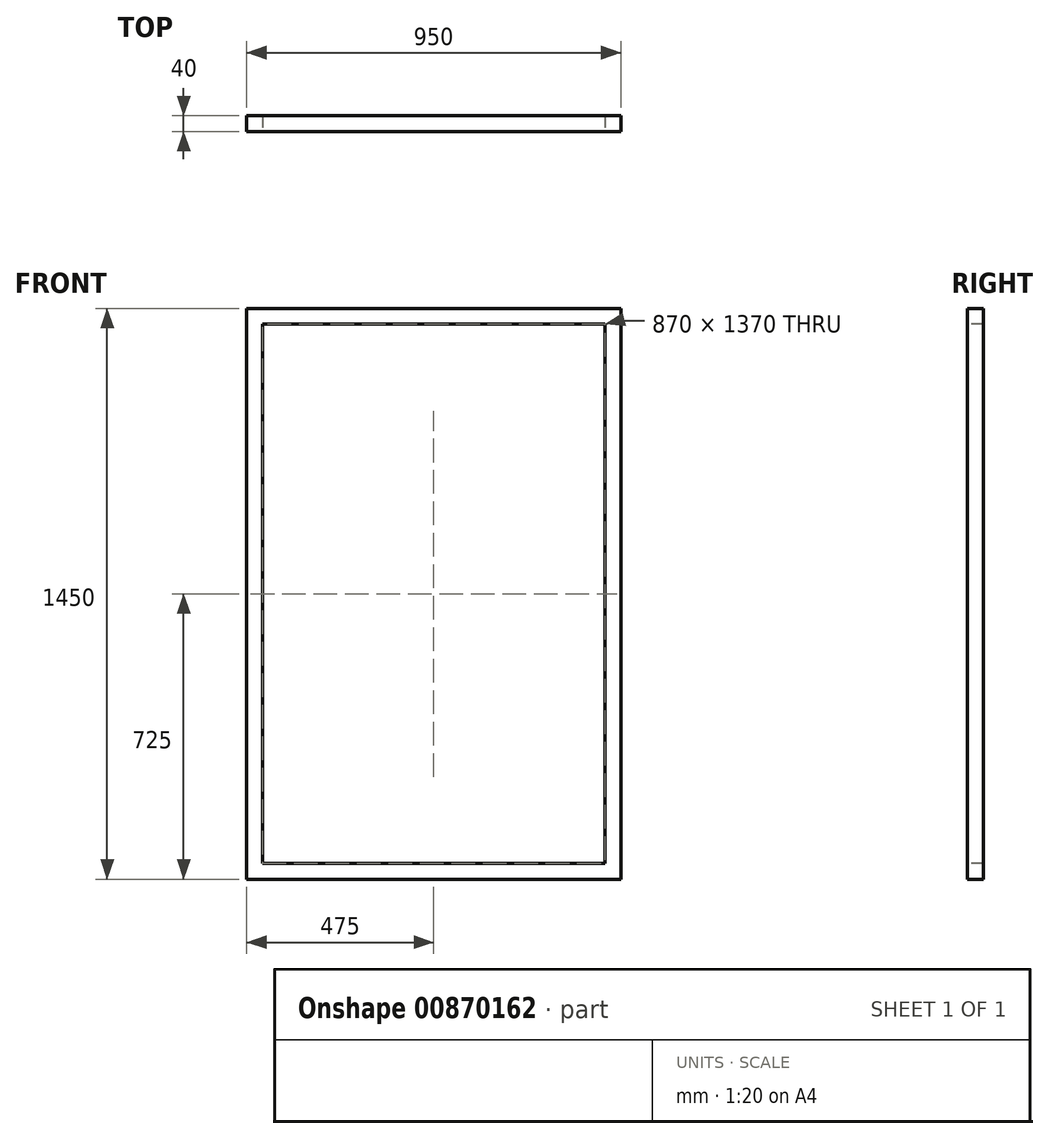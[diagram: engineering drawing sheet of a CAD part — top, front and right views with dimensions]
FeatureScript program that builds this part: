
annotation { "Feature Type Name" : "Feature", "Feature Type Description" : "" }
export const myFeature = defineFeature(function(context is Context, id is Id, definition is map)
    precondition{}
    {
        {
            var Q0;
            Q0=qCreatedBy(makeId("Front.planeOp"),FACE);
            var sketch = newSketch(context, id + "F0", { "sketchPlane" : qUnion([Q0])});
            skLineSegment(sketch, "E0.bottom", {"start": v(0, 0) * mm, "end": v(950, 0) * mm});
            skLineSegment(sketch, "E0.top", {"start": v(0, 1450) * mm, "end": v(950, 1450) * mm});
            skLineSegment(sketch, "E0.left", {"start": v(0, 0) * mm, "end": v(0, 1450) * mm});
            skLineSegment(sketch, "E0.right", {"start": v(950, 0) * mm, "end": v(950, 1450) * mm});
            skLineSegment(sketch, "E1.bottom", {"start": v(40, 40) * mm, "end": v(910, 40) * mm});
            skLineSegment(sketch, "E1.top", {"start": v(40, 1410) * mm, "end": v(910, 1410) * mm});
            skLineSegment(sketch, "E1.left", {"start": v(40, 40) * mm, "end": v(40, 1410) * mm});
            skLineSegment(sketch, "E1.right", {"start": v(910, 40) * mm, "end": v(910, 1410) * mm});
            skLineSegment(sketch, "E2", {"start": v(0, 40) * mm, "end": v(40, 40) * mm, "construction": true});
            skLineSegment(sketch, "E3", {"start": v(40, 40) * mm, "end": v(40, 0) * mm, "construction": true});
            skLineSegment(sketch, "E4", {"start": v(910, 1410) * mm, "end": v(910, 1450) * mm, "construction": true});
            skLineSegment(sketch, "E5", {"start": v(910, 1410) * mm, "end": v(950, 1410) * mm, "construction": true});
            skSolve(sketch);
        }
        {
            var Q0;
            Q0 = qSketchRegion(id + "F0", true);
            extrude(context, id + "F1", {"entities" : qUnion([Q0]), "oppositeDirection" : true, "depth" : 40 * mm, "offsetDistance" : 25 * mm});
        }
    });
